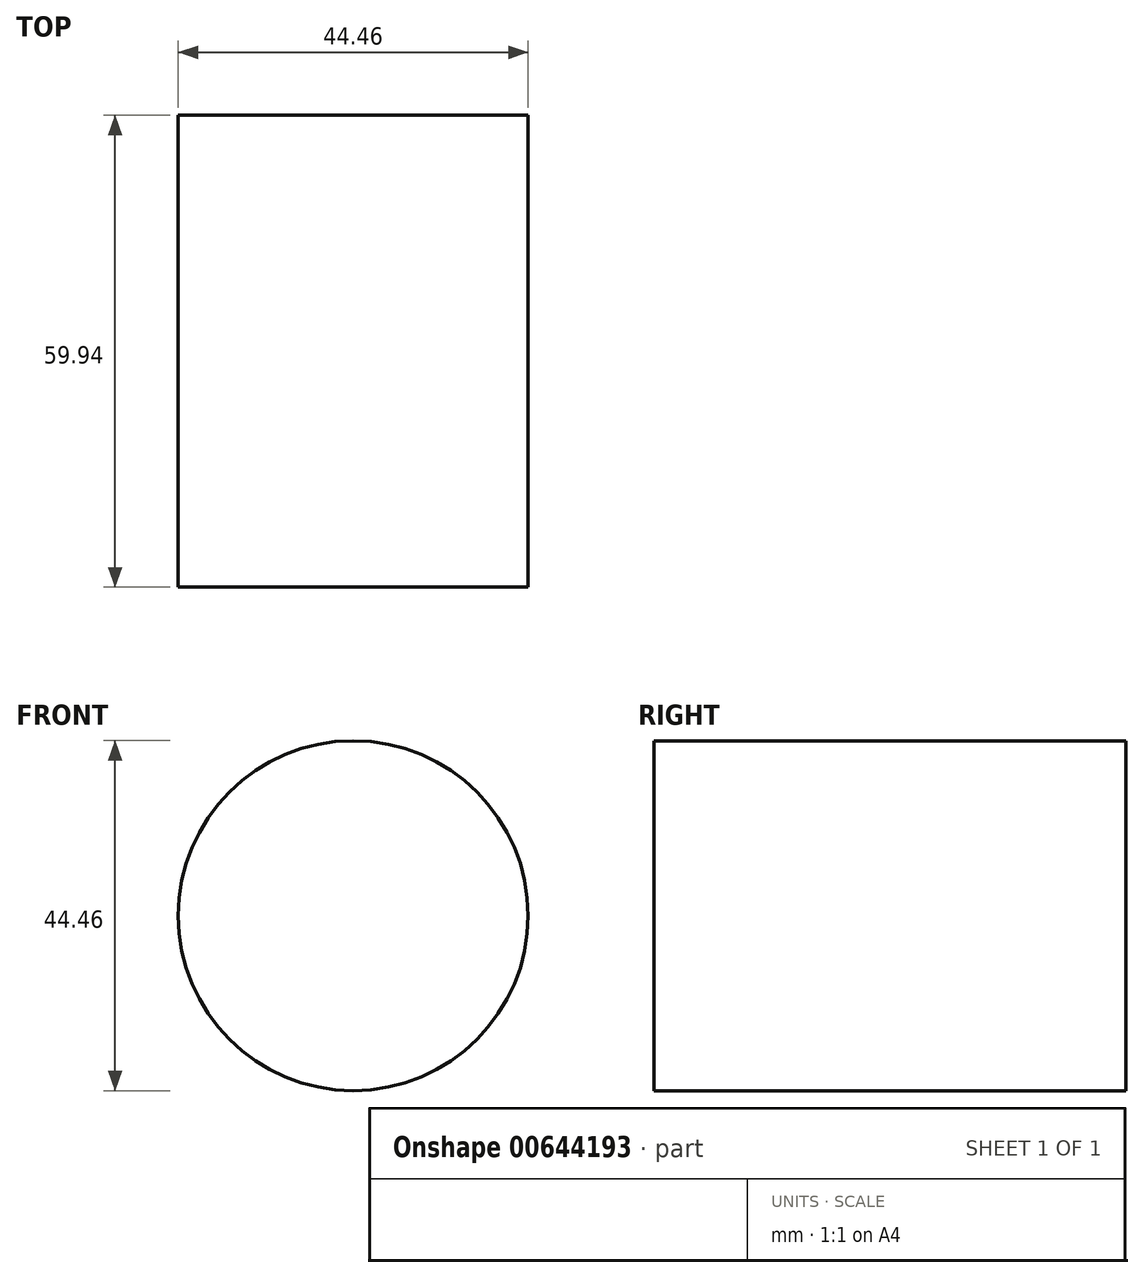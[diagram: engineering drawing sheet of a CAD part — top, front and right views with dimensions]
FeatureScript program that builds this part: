
annotation { "Feature Type Name" : "Feature", "Feature Type Description" : "" }
export const myFeature = defineFeature(function(context is Context, id is Id, definition is map)
    precondition{}
    {
        {
            var Q0;
            Q0=qCreatedBy(makeId("Front.planeOp"),FACE);
            var sketch = newSketch(context, id + "F0", { "sketchPlane" : qUnion([Q0])});
            skCircle(sketch, "E0", {"center": v(0, 0) * mm, "radius": 22.23 * mm});
            skSolve(sketch);
        }
        {
            var Q0;
            Q0=makeQuery(id+"F0.imprint","IMPRINT",FACE,{"disambiguationData":[TD([[makeQuery(id+"F0.imprint","IMPRINT",EDGE,{"derivedFrom":sQuery(id+"F0.wireOp",EDGE,"E0")}),1.0]])]});
            extrude(context, id + "F1", {"entities" : qUnion([Q0]), "depth" : 59.94 * mm, "offsetDistance" : 25.4 * mm});
        }
    });
